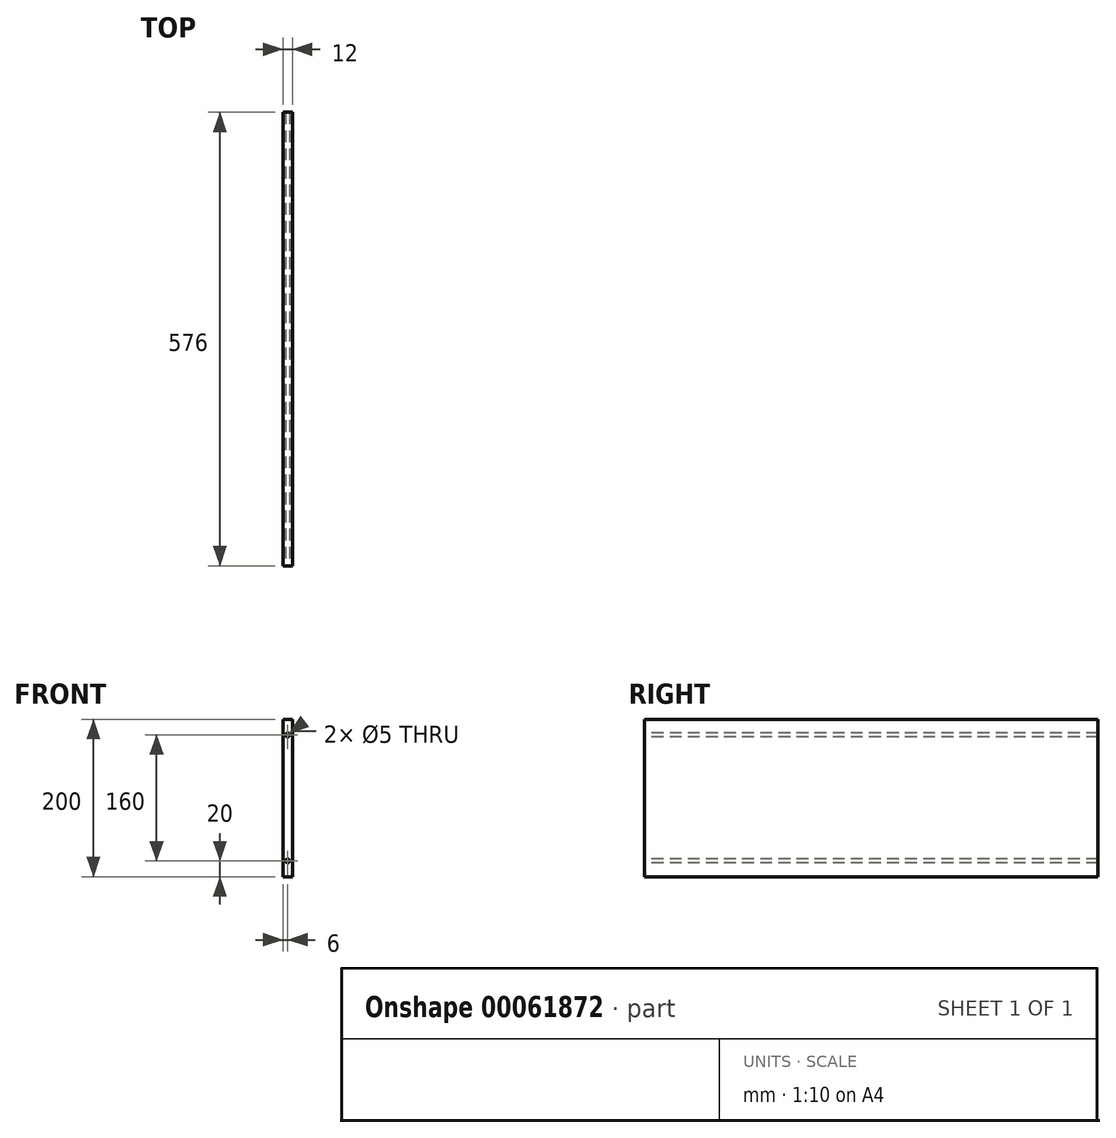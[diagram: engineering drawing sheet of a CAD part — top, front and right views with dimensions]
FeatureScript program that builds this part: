
annotation { "Feature Type Name" : "Feature", "Feature Type Description" : "" }
export const myFeature = defineFeature(function(context is Context, id is Id, definition is map)
    precondition{}
    {
        {
            var Q0;
            Q0=qCreatedBy(makeId("Right.planeOp"),FACE);
            var sketch = newSketch(context, id + "F0", { "sketchPlane" : qUnion([Q0])});
            skLineSegment(sketch, "E0.bottom", {"start": v(0, 0) * mm, "end": v(576, 0) * mm});
            skLineSegment(sketch, "E0.top", {"start": v(0, -200) * mm, "end": v(576, -200) * mm});
            skLineSegment(sketch, "E0.left", {"start": v(0, 0) * mm, "end": v(0, -200) * mm});
            skLineSegment(sketch, "E0.right", {"start": v(576, 0) * mm, "end": v(576, -200) * mm});
            skSolve(sketch);
        }
        {
            var Q0;
            Q0=makeQuery(id+"F0.imprint","IMPRINT",FACE,{"disambiguationData":[TD([[makeQuery(id+"F0.imprint","IMPRINT",EDGE,{"derivedFrom":sQuery(id+"F0.wireOp",EDGE,"E0.bottom")}),-1.0]])]});
            extrude(context, id + "F1", {"entities" : qUnion([Q0]), "depth" : 12 * mm});
        }
        {
            var Q0;
            Q0=makeQuery(id+"F1.opExtrude","SWEPT_FACE",FACE,{"disambiguationData":[OSD([sQuery(id+"F0.wireOp",EDGE,"E0.left")])]});
            var sketch = newSketch(context, id + "F2", { "sketchPlane" : qUnion([Q0])});
            skPoint(sketch, "E1", {"position": v(6, -20) * mm});
            skPoint(sketch, "E2", {"position": v(6, -180) * mm});
            skSolve(sketch);
        }
        {
            var Q0;
            Q0=sQuery(id+"F2.wireOp",VERTEX,"E1");
            var Q1;
            Q1=sQuery(id+"F2.wireOp",VERTEX,"E2");
            var Q2;
            Q2=makeQuery(id+"F1.opExtrude","SWEPT_BODY",BODY,{"disambiguationData":[OSD([sQuery(id+"F0.wireOp",EDGE,"E0.bottom"),sQuery(id+"F0.wireOp",EDGE,"E0.top"),sQuery(id+"F0.wireOp",EDGE,"E0.left"),sQuery(id+"F0.wireOp",EDGE,"E0.right")])]});
            hole(context, id + "F3", {"style" : HoleStyle.SIMPLE, "holeDiameter" : 5 * mm, "endStyle" : HoleEndStyle.THROUGH, "locations" : qUnion([Q0, Q1]), "scope" : qUnion([Q2])});
        }
    });
